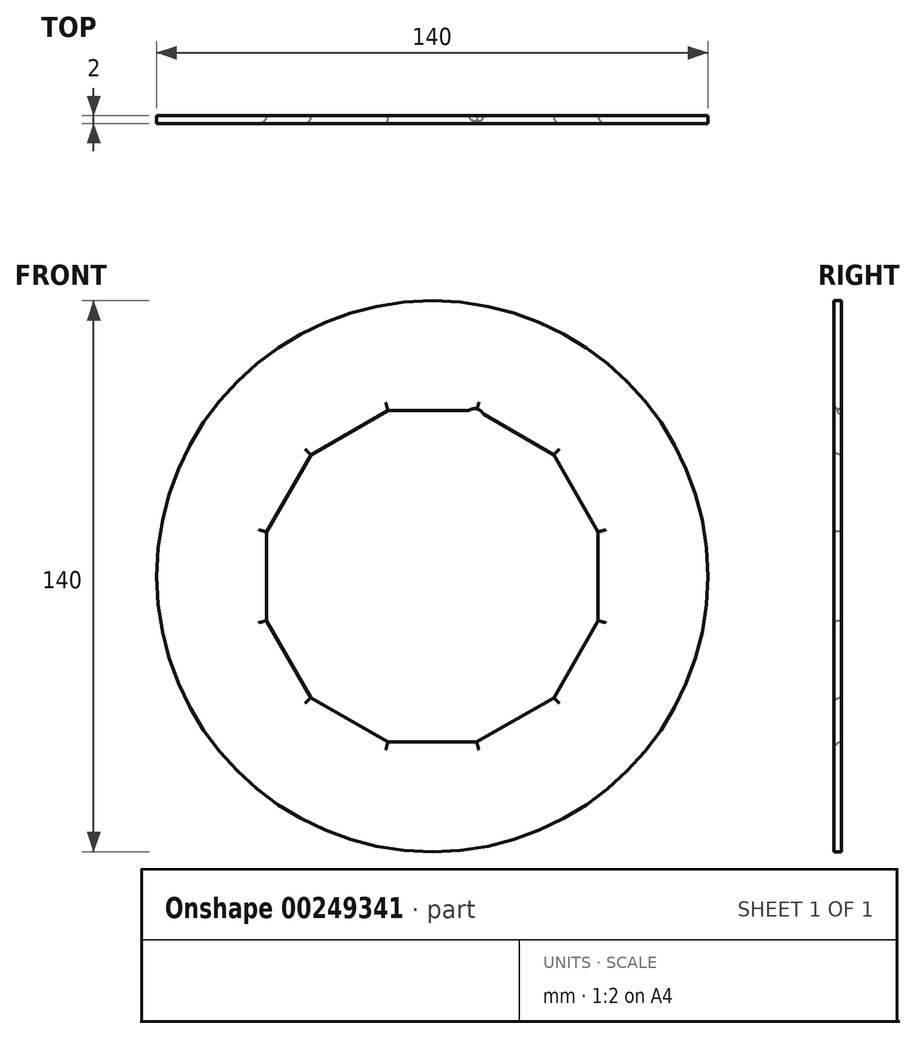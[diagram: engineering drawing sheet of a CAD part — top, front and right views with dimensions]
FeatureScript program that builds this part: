
annotation { "Feature Type Name" : "Feature", "Feature Type Description" : "" }
export const myFeature = defineFeature(function(context is Context, id is Id, definition is map)
    precondition{}
    {
        {
            var Q0;
            Q0=qCreatedBy(makeId("Front.planeOp"),FACE);
            var sketch = newSketch(context, id + "F0", { "sketchPlane" : qUnion([Q0])});
            skCircle(sketch, "E0.cCircle", {"center": v(0, 0) * mm, "radius": 42.15 * mm, "construction": true});
            skLineSegment(sketch, "E0.0", {"start": v(-11.3, 42.15) * mm, "end": v(11.3, 42.15) * mm});
            skLineSegment(sketch, "E0.1", {"start": v(11.3, 42.15) * mm, "end": v(30.86, 30.86) * mm});
            skLineSegment(sketch, "E0.2", {"start": v(30.86, 30.86) * mm, "end": v(42.15, 11.3) * mm});
            skLineSegment(sketch, "E0.3", {"start": v(42.15, 11.3) * mm, "end": v(42.15, -11.3) * mm});
            skLineSegment(sketch, "E0.4", {"start": v(42.15, -11.3) * mm, "end": v(30.86, -30.86) * mm});
            skLineSegment(sketch, "E0.5", {"start": v(30.86, -30.86) * mm, "end": v(11.3, -42.15) * mm});
            skLineSegment(sketch, "E0.6", {"start": v(11.3, -42.15) * mm, "end": v(-11.3, -42.15) * mm});
            skLineSegment(sketch, "E0.7", {"start": v(-11.3, -42.15) * mm, "end": v(-30.86, -30.86) * mm});
            skLineSegment(sketch, "E0.8", {"start": v(-30.86, -30.86) * mm, "end": v(-42.15, -11.3) * mm});
            skLineSegment(sketch, "E0.9", {"start": v(-42.15, -11.3) * mm, "end": v(-42.15, 11.3) * mm});
            skLineSegment(sketch, "E0.10", {"start": v(-42.15, 11.3) * mm, "end": v(-30.86, 30.86) * mm});
            skLineSegment(sketch, "E0.11", {"start": v(-30.86, 30.86) * mm, "end": v(-11.3, 42.15) * mm});
            skPoint(sketch, "E0.0.midPoint", {"position": v(0, 42.15) * mm});
            skCircle(sketch, "E1", {"center": v(0, 0) * mm, "radius": 70 * mm});
            skSolve(sketch);
        }
        {
            var Q0;
            Q0=makeQuery(id+"F0.imprint","IMPRINT",FACE,{"disambiguationData":[TD([[makeQuery(id+"F0.imprint","IMPRINT",EDGE,{"derivedFrom":sQuery(id+"F0.wireOp",EDGE,"E0.0")}),1.0]])]});
            extrude(context, id + "F1", {"entities" : qUnion([Q0]), "depth" : 2 * mm, "symmetric" : true});
        }
        {
            var Q0;
            Q0=qCreatedBy(makeId("Front.planeOp"),FACE);
            var sketch = newSketch(context, id + "F2", { "sketchPlane" : qUnion([Q0])});
            skCircle(sketch, "E2", {"center": v(10.74, 40.09) * mm, "radius": 2.5 * mm});
            skLineSegment(sketch, "E3", {"start": v(10.74, 40.09) * mm, "end": v(0, 0) * mm, "construction": true});
            skSolve(sketch);
        }
        {
            var Q0;
            Q0=makeQuery(id+"F1.opExtrude","CAP_EDGE",EDGE,{"disambiguationData":[OSD([sQuery(id+"F0.wireOp",EDGE,"E0.11")])],"isStart":false});
            var Q1;
            Q1=makeQuery(id+"F1.opExtrude","CAP_EDGE",EDGE,{"disambiguationData":[OSD([sQuery(id+"F0.wireOp",EDGE,"E0.0")])],"isStart":false});
            var Q2;
            Q2=makeQuery(id+"F1.opExtrude","CAP_EDGE",EDGE,{"disambiguationData":[OSD([sQuery(id+"F0.wireOp",EDGE,"E0.1")])],"isStart":false});
            var Q3;
            Q3=makeQuery(id+"F1.opExtrude","CAP_EDGE",EDGE,{"disambiguationData":[OSD([sQuery(id+"F0.wireOp",EDGE,"E0.2")])],"isStart":false});
            var Q4;
            Q4=makeQuery(id+"F1.opExtrude","CAP_EDGE",EDGE,{"disambiguationData":[OSD([sQuery(id+"F0.wireOp",EDGE,"E0.3")])],"isStart":false});
            var Q5;
            Q5=makeQuery(id+"F1.opExtrude","CAP_EDGE",EDGE,{"disambiguationData":[OSD([sQuery(id+"F0.wireOp",EDGE,"E0.4")])],"isStart":false});
            var Q6;
            Q6=makeQuery(id+"F1.opExtrude","CAP_EDGE",EDGE,{"disambiguationData":[OSD([sQuery(id+"F0.wireOp",EDGE,"E0.5")])],"isStart":false});
            var Q7;
            Q7=makeQuery(id+"F1.opExtrude","CAP_EDGE",EDGE,{"disambiguationData":[OSD([sQuery(id+"F0.wireOp",EDGE,"E0.6")])],"isStart":false});
            var Q8;
            Q8=makeQuery(id+"F1.opExtrude","CAP_EDGE",EDGE,{"disambiguationData":[OSD([sQuery(id+"F0.wireOp",EDGE,"E0.7")])],"isStart":false});
            var Q9;
            Q9=makeQuery(id+"F1.opExtrude","CAP_EDGE",EDGE,{"disambiguationData":[OSD([sQuery(id+"F0.wireOp",EDGE,"E0.8")])],"isStart":false});
            var Q10;
            Q10=makeQuery(id+"F1.opExtrude","CAP_EDGE",EDGE,{"disambiguationData":[OSD([sQuery(id+"F0.wireOp",EDGE,"E0.9")])],"isStart":false});
            var Q11;
            Q11=makeQuery(id+"F1.opExtrude","CAP_EDGE",EDGE,{"disambiguationData":[OSD([sQuery(id+"F0.wireOp",EDGE,"E0.10")])],"isStart":false});
            fillet(context, id + "F3", {"entities" : qUnion([Q0, Q1, Q2, Q3, Q4, Q5, Q6, Q7, Q8, Q9, Q10, Q11]), "radius" : 2 * mm, "tangentPropagation" : true, "allowEdgeOverflow" : false});
        }
        {
            var Q0;
            Q0=makeQuery(id+"F2.imprint","IMPRINT",FACE,{"disambiguationData":[TD([[makeQuery(id+"F2.imprint","IMPRINT",EDGE,{"derivedFrom":sQuery(id+"F2.wireOp",EDGE,"E2")}),1.0]])]});
            extrude(context, id + "F4", {"entities" : qUnion([Q0]), "operationType" : NewBodyOperationType.REMOVE, "depth" : 25 * mm, "symmetric" : true});
        }
    });
